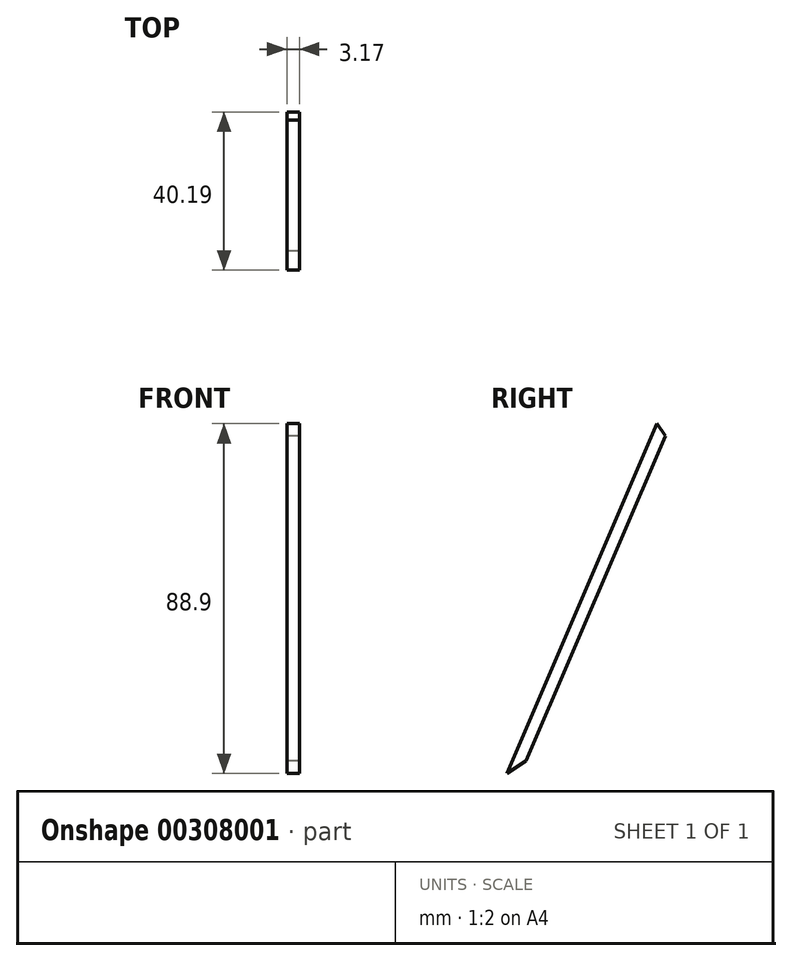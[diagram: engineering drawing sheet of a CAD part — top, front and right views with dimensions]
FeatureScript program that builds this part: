
annotation { "Feature Type Name" : "Feature", "Feature Type Description" : "" }
export const myFeature = defineFeature(function(context is Context, id is Id, definition is map)
    precondition{}
    {
        {
            var Q0;
            Q0=qCreatedBy(makeId("Right.planeOp"),FACE);
            var sketch = newSketch(context, id + "F0", { "sketchPlane" : qUnion([Q0])});
            skLineSegment(sketch, "E0", {"start": v(0, 0) * mm, "end": v(38.1, 88.9) * mm});
            skLineSegment(sketch, "E1.0", {"start": v(4.82, 3.18) * mm, "end": v(40.2, 85.73) * mm});
            skLineSegment(sketch, "E2", {"start": v(4.82, 3.18) * mm, "end": v(0, 0) * mm});
            skLineSegment(sketch, "E3", {"start": v(38.1, 88.9) * mm, "end": v(40.2, 85.73) * mm});
            skSolve(sketch);
        }
        {
            var Q0;
            Q0=makeQuery(id+"F0.imprint","IMPRINT",FACE,{"disambiguationData":[TD([[makeQuery(id+"F0.imprint","IMPRINT",EDGE,{"derivedFrom":sQuery(id+"F0.wireOp",EDGE,"E0")}),-1.0]])]});
            extrude(context, id + "F1", {"entities" : qUnion([Q0]), "depth" : 3.17 * mm});
        }
    });
